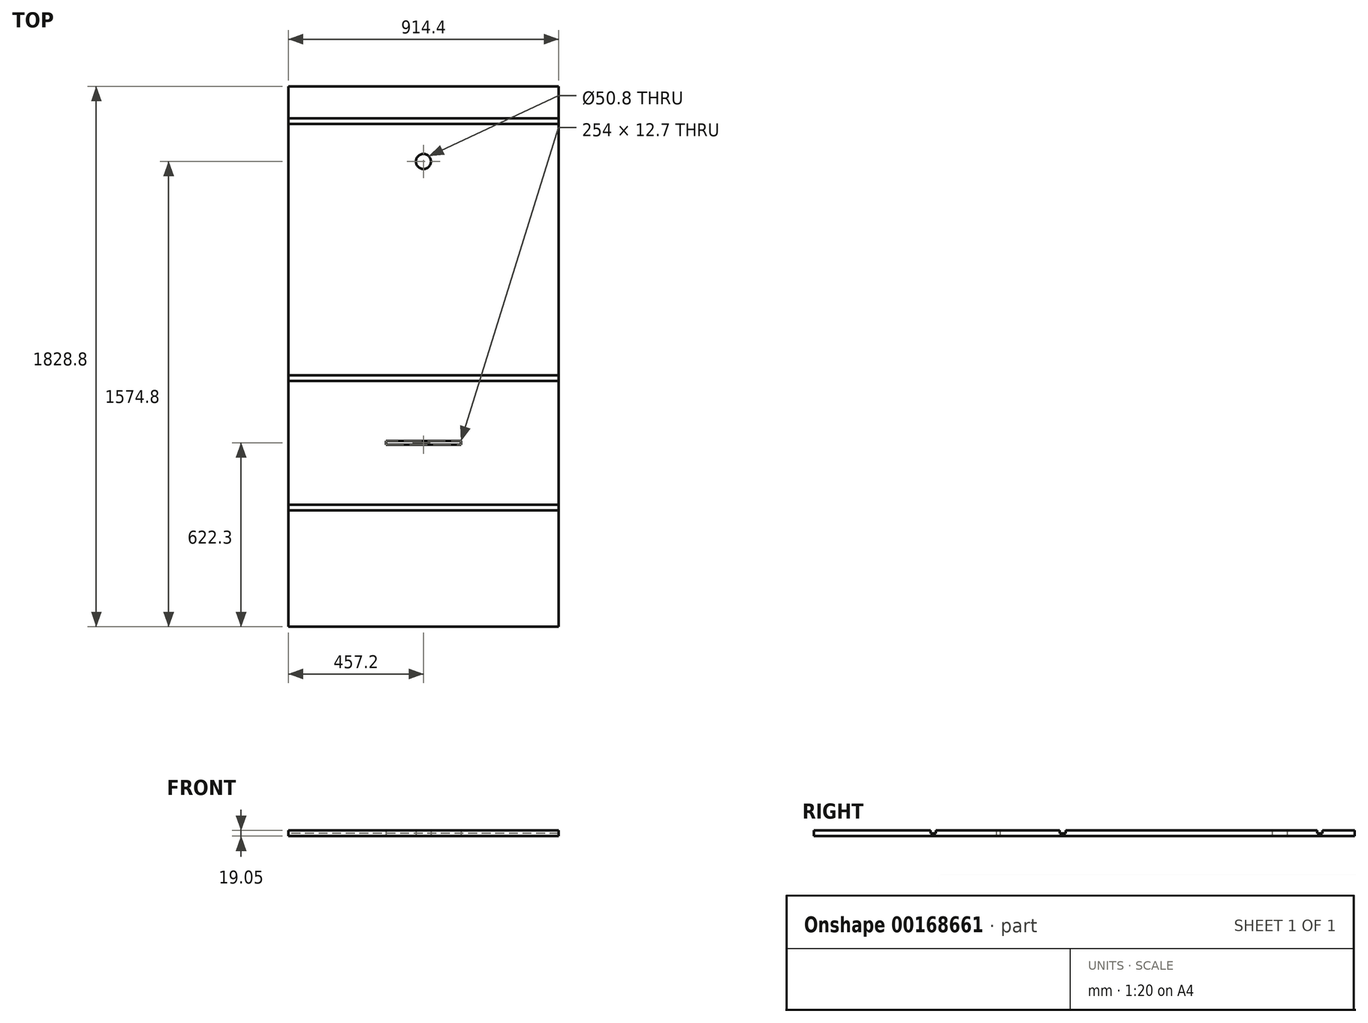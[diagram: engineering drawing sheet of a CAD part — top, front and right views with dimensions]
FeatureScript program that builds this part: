
annotation { "Feature Type Name" : "Feature", "Feature Type Description" : "" }
export const myFeature = defineFeature(function(context is Context, id is Id, definition is map)
    precondition{}
    {
        {
            var Q0;
            Q0=qCreatedBy(makeId("Top.planeOp"),FACE);
            var sketch = newSketch(context, id + "F0", { "sketchPlane" : qUnion([Q0])});
            skLineSegment(sketch, "E0.bottom", {"start": v(0, 0) * mm, "end": v(914.4, 0) * mm});
            skLineSegment(sketch, "E0.top", {"start": v(0, 1828.8) * mm, "end": v(914.4, 1828.8) * mm});
            skLineSegment(sketch, "E0.left", {"start": v(0, 0) * mm, "end": v(0, 1828.8) * mm});
            skLineSegment(sketch, "E0.right", {"start": v(914.4, 0) * mm, "end": v(914.4, 1828.8) * mm});
            skPoint(sketch, "E1", {"position": v(457.2, 0) * mm});
            skPoint(sketch, "E2", {"position": v(457.2, 622.3) * mm});
            skLineSegment(sketch, "E3", {"start": v(457.2, 622.3) * mm, "end": v(584.2, 622.3) * mm});
            skLineSegment(sketch, "E4", {"start": v(457.2, 622.3) * mm, "end": v(330.2, 622.3) * mm});
            skLineSegment(sketch, "E5", {"start": v(330.2, 622.3) * mm, "end": v(330.2, 628.65) * mm});
            skLineSegment(sketch, "E6", {"start": v(584.2, 622.3) * mm, "end": v(584.2, 615.95) * mm});
            skLineSegment(sketch, "E7.bottom", {"start": v(330.2, 628.65) * mm, "end": v(584.2, 628.65) * mm});
            skLineSegment(sketch, "E7.top", {"start": v(330.2, 615.95) * mm, "end": v(584.2, 615.95) * mm});
            skLineSegment(sketch, "E7.left", {"start": v(330.2, 628.65) * mm, "end": v(330.2, 615.95) * mm});
            skLineSegment(sketch, "E7.right", {"start": v(584.2, 628.65) * mm, "end": v(584.2, 615.95) * mm});
            skLineSegment(sketch, "E8", {"start": v(457.2, 615.95) * mm, "end": v(457.2, 412.75) * mm});
            skLineSegment(sketch, "E9", {"start": v(457.2, 628.65) * mm, "end": v(457.2, 831.85) * mm});
            skPoint(sketch, "E10", {"position": v(0, 412.75) * mm});
            skPoint(sketch, "E11", {"position": v(0, 831.85) * mm});
            skLineSegment(sketch, "E12.bottom", {"start": v(0, 412.75) * mm, "end": v(914.4, 412.75) * mm});
            skLineSegment(sketch, "E12.top", {"start": v(0, 393.7) * mm, "end": v(914.4, 393.7) * mm});
            skLineSegment(sketch, "E12.left", {"start": v(0, 412.75) * mm, "end": v(0, 393.7) * mm});
            skLineSegment(sketch, "E12.right", {"start": v(914.4, 412.75) * mm, "end": v(914.4, 393.7) * mm});
            skLineSegment(sketch, "E13.bottom", {"start": v(0, 831.85) * mm, "end": v(914.4, 831.85) * mm});
            skLineSegment(sketch, "E13.top", {"start": v(0, 850.9) * mm, "end": v(914.4, 850.9) * mm});
            skLineSegment(sketch, "E13.left", {"start": v(0, 831.85) * mm, "end": v(0, 850.9) * mm});
            skLineSegment(sketch, "E13.right", {"start": v(914.4, 831.85) * mm, "end": v(914.4, 850.9) * mm});
            skPoint(sketch, "E14", {"position": v(457.2, 1828.8) * mm});
            skPoint(sketch, "E15", {"position": v(457.2, 1574.8) * mm});
            skPoint(sketch, "E16", {"position": v(457.2, 1701.8) * mm});
            skPoint(sketch, "E17", {"position": v(0, 1701.8) * mm});
            skLineSegment(sketch, "E18.bottom", {"start": v(0, 1701.8) * mm, "end": v(914.4, 1701.8) * mm});
            skLineSegment(sketch, "E18.top", {"start": v(0, 1720.85) * mm, "end": v(914.4, 1720.85) * mm});
            skLineSegment(sketch, "E18.left", {"start": v(0, 1701.8) * mm, "end": v(0, 1720.85) * mm});
            skLineSegment(sketch, "E18.right", {"start": v(914.4, 1701.8) * mm, "end": v(914.4, 1720.85) * mm});
            skCircle(sketch, "E19", {"center": v(457.2, 1574.8) * mm, "radius": 25.4 * mm});
            skSolve(sketch);
        }
        {
            var Q0;
            {var subQ2=sQuery(id+"F0.wireOp",EDGE,"E0.top");Q0=makeQuery(id+"F0.imprint","IMPRINT",FACE,{"disambiguationData":[TD([[makeQuery(id+"F0.imprint","IMPRINT",EDGE,{"derivedFrom":subQ2}),-1.0]])]});}
            var Q1;
            {var subQ1=sQuery(id+"F0.wireOp",EDGE,"E13.top");Q1=makeQuery(id+"F0.imprint","IMPRINT",FACE,{"disambiguationData":[TD([[makeQuery(id+"F0.imprint","IMPRINT",EDGE,{"derivedFrom":subQ1}),1.0]])]});}
            var Q2;
            {var subQ6=sQuery(id+"F0.wireOp",EDGE,"E8");Q2=makeQuery(id+"F0.imprint","IMPRINT",FACE,{"disambiguationData":[TD([[makeQuery(id+"F0.imprint","IMPRINT",EDGE,{"derivedFrom":subQ6}),-1.0]])]});}
            var Q3;
            {var subQ6=sQuery(id+"F0.wireOp",EDGE,"E8");Q3=makeQuery(id+"F0.imprint","IMPRINT",FACE,{"disambiguationData":[TD([[makeQuery(id+"F0.imprint","IMPRINT",EDGE,{"derivedFrom":subQ6}),1.0]])]});}
            var Q4;
            {var subQ2=sQuery(id+"F0.wireOp",EDGE,"E0.bottom");Q4=makeQuery(id+"F0.imprint","IMPRINT",FACE,{"disambiguationData":[TD([[makeQuery(id+"F0.imprint","IMPRINT",EDGE,{"derivedFrom":subQ2}),1.0]])]});}
            var Q5;
            Q5=makeQuery(id+"F0.imprint","IMPRINT",FACE,{"disambiguationData":[TD([[makeQuery(id+"F0.imprint","IMPRINT",EDGE,{"derivedFrom":sQuery(id+"F0.wireOp",EDGE,"E13.top")}),-1.0]])]});
            var Q6;
            Q6=makeQuery(id+"F0.imprint","IMPRINT",FACE,{"disambiguationData":[TD([[makeQuery(id+"F0.imprint","IMPRINT",EDGE,{"derivedFrom":sQuery(id+"F0.wireOp",EDGE,"E12.top")}),1.0]])]});
            var Q7;
            Q7=makeQuery(id+"F0.imprint","IMPRINT",FACE,{"disambiguationData":[TD([[makeQuery(id+"F0.imprint","IMPRINT",EDGE,{"derivedFrom":sQuery(id+"F0.wireOp",EDGE,"E18.bottom")}),1.0]])]});
            extrude(context, id + "F1", {"entities" : qUnion([Q0, Q1, Q2, Q3, Q4, Q5, Q6, Q7]), "depth" : 9.52 * mm});
        }
        {
            var Q0;
            {var subQ2=sQuery(id+"F0.wireOp",EDGE,"E0.top");Q0=makeQuery(id+"F0.imprint","IMPRINT",FACE,{"disambiguationData":[TD([[makeQuery(id+"F0.imprint","IMPRINT",EDGE,{"derivedFrom":subQ2}),-1.0]])]});}
            var Q1;
            {var subQ1=sQuery(id+"F0.wireOp",EDGE,"E13.top");Q1=makeQuery(id+"F0.imprint","IMPRINT",FACE,{"disambiguationData":[TD([[makeQuery(id+"F0.imprint","IMPRINT",EDGE,{"derivedFrom":subQ1}),1.0]])]});}
            var Q2;
            {var subQ6=sQuery(id+"F0.wireOp",EDGE,"E8");Q2=makeQuery(id+"F0.imprint","IMPRINT",FACE,{"disambiguationData":[TD([[makeQuery(id+"F0.imprint","IMPRINT",EDGE,{"derivedFrom":subQ6}),-1.0]])]});}
            var Q3;
            {var subQ6=sQuery(id+"F0.wireOp",EDGE,"E8");Q3=makeQuery(id+"F0.imprint","IMPRINT",FACE,{"disambiguationData":[TD([[makeQuery(id+"F0.imprint","IMPRINT",EDGE,{"derivedFrom":subQ6}),1.0]])]});}
            var Q4;
            {var subQ2=sQuery(id+"F0.wireOp",EDGE,"E0.bottom");Q4=makeQuery(id+"F0.imprint","IMPRINT",FACE,{"disambiguationData":[TD([[makeQuery(id+"F0.imprint","IMPRINT",EDGE,{"derivedFrom":subQ2}),1.0]])]});}
            extrude(context, id + "F2", {"entities" : qUnion([Q0, Q1, Q2, Q3, Q4]), "operationType" : NewBodyOperationType.ADD, "depth" : 19.05 * mm});
        }
    });
